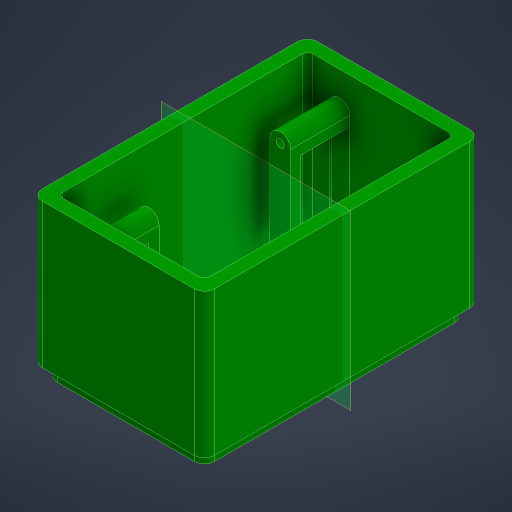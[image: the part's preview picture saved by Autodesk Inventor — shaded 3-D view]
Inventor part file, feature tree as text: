
AUTODESK INVENTOR PART (.ipt)
format: ipt  version: 2024 (Build 280153000, 153)  size: 264,704 bytes
history: native  units: mm
features: reference x18, other x8, extrude x3, sketch x3, shell x2, mirror x1
ambient origin geometry x8: Origin, YZ Plane, XZ Plane, XY Plane, X Axis, Y Axis, Z Axis, Center Point
bodies: Body1 (feature_tree)
feature tree (35):
  other  "Твердое тело1"
  extrude  "Выдавливание1"  Depth=2.0mm
  extrude  "Выдавливание2"  Depth=5.0mm TaperAngle=0.0deg
  sketch  "Эскиз3"
  other  "РабПлоскость1"
  extrude  "Выдавливание3"  Depth=56.0mm TaperAngle=0.0deg
  shell  "Оболочка1"  Thickness=8.0mm
  other  "РабПлоскость2"
  mirror  "Зеркальное отражение1"
  shell  "Оболочка2"  Thickness=56.0mm
  sketch  "Эскиз1"
  reference  "Ссылка1"
  reference  "Ссылка2"
  reference  "Ссылка3"
  reference  "Ссылка4"
  reference  "Ссылка5"
  reference  "Ссылка6"
  reference  "Ссылка7"
  reference  "Ссылка8"
  sketch  "Эскиз2"
  reference  "Ссылка9"
  reference  "Ссылка10"
  reference  "Ссылка11"
  reference  "Ссылка12"
  reference  "Ссылка13"
  reference  "Ссылка14"
  reference  "Ссылка15"
  reference  "Ссылка16"
  reference  "Ссылка17"
  reference  "Ссылка18"
  parser-record x1  (decoder bookkeeping rows leaked as tree rows — omitted from the tree; the rows remain in map.json)
  other  "back_box_asembly.iam"
  other  "back_box:1"
  other  "BTS7960:2"
  other  "PCB, BTS7960 43A HIGH POWER H BRIDGE MODULE_1"
note: 1 file-system path scrubbed to <path> (originals preserved in map.json)
